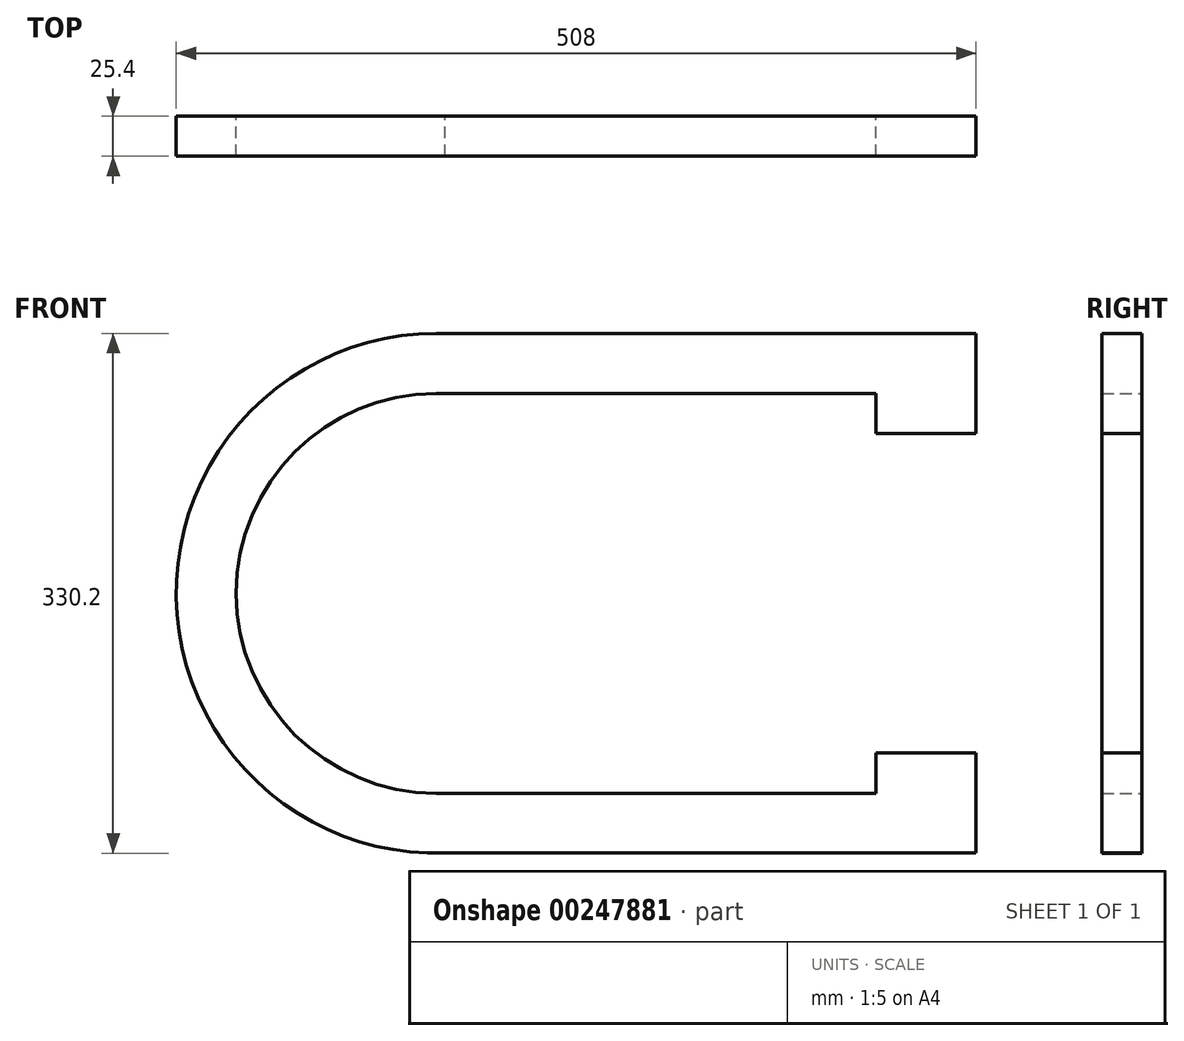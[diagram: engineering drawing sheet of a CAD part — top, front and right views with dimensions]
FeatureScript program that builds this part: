
annotation { "Feature Type Name" : "Feature", "Feature Type Description" : "" }
export const myFeature = defineFeature(function(context is Context, id is Id, definition is map)
    precondition{}
    {
        {
            var Q0;
            Q0=qCreatedBy(makeId("Front.planeOp"),FACE);
            var sketch = newSketch(context, id + "F0", { "sketchPlane" : qUnion([Q0])});
            skArc(sketch, "E0", {"start": v(0, 127) * mm, "mid": v(-127, 0) * mm, "end": v(0, -127) * mm});
            skArc(sketch, "E1", {"start": v(0, 165.1) * mm, "mid": v(-165.08, -2.78) * mm, "end": v(5.56, -165) * mm});
            skLineSegment(sketch, "E2", {"start": v(0, 165.1) * mm, "end": v(342.9, 165.1) * mm});
            skLineSegment(sketch, "E3", {"start": v(342.9, -165) * mm, "end": v(0, -165) * mm});
            skLineSegment(sketch, "E4", {"start": v(0, 127) * mm, "end": v(279.4, 127) * mm});
            skLineSegment(sketch, "E5", {"start": v(342.9, 127) * mm, "end": v(342.9, 165.1) * mm});
            skLineSegment(sketch, "E6", {"start": v(0, -127) * mm, "end": v(279.4, -127) * mm});
            skLineSegment(sketch, "E7.bottom", {"start": v(342.9, -165) * mm, "end": v(279.4, -165) * mm});
            skLineSegment(sketch, "E7.top", {"start": v(342.9, -101.5) * mm, "end": v(279.4, -101.5) * mm});
            skLineSegment(sketch, "E7.left", {"start": v(342.9, -165) * mm, "end": v(342.9, -101.5) * mm});
            skLineSegment(sketch, "E7.right", {"start": v(279.4, -127) * mm, "end": v(279.4, -101.5) * mm});
            skLineSegment(sketch, "E8.trimOffspring", {"start": v(342.9, -127) * mm, "end": v(345.57, -127) * mm});
            skLineSegment(sketch, "E9.bottom", {"start": v(342.9, 165.1) * mm, "end": v(279.4, 165.1) * mm});
            skLineSegment(sketch, "E9.top", {"start": v(342.9, 101.6) * mm, "end": v(279.4, 101.6) * mm});
            skLineSegment(sketch, "E9.left", {"start": v(342.9, 165.1) * mm, "end": v(342.9, 101.6) * mm});
            skLineSegment(sketch, "E9.right", {"start": v(279.4, 127) * mm, "end": v(279.4, 101.6) * mm});
            skSolve(sketch);
        }
        {
            var Q0;
            Q0=makeQuery(id+"F0.imprint","IMPRINT",FACE,{"disambiguationData":[TD([[makeQuery(id+"F0.imprint","IMPRINT",EDGE,{"derivedFrom":sQuery(id+"F0.wireOp",EDGE,"E0")}),-1.0]])]});
            extrude(context, id + "F1", {"entities" : qUnion([Q0]), "depth" : 25.4 * mm});
        }
    });
